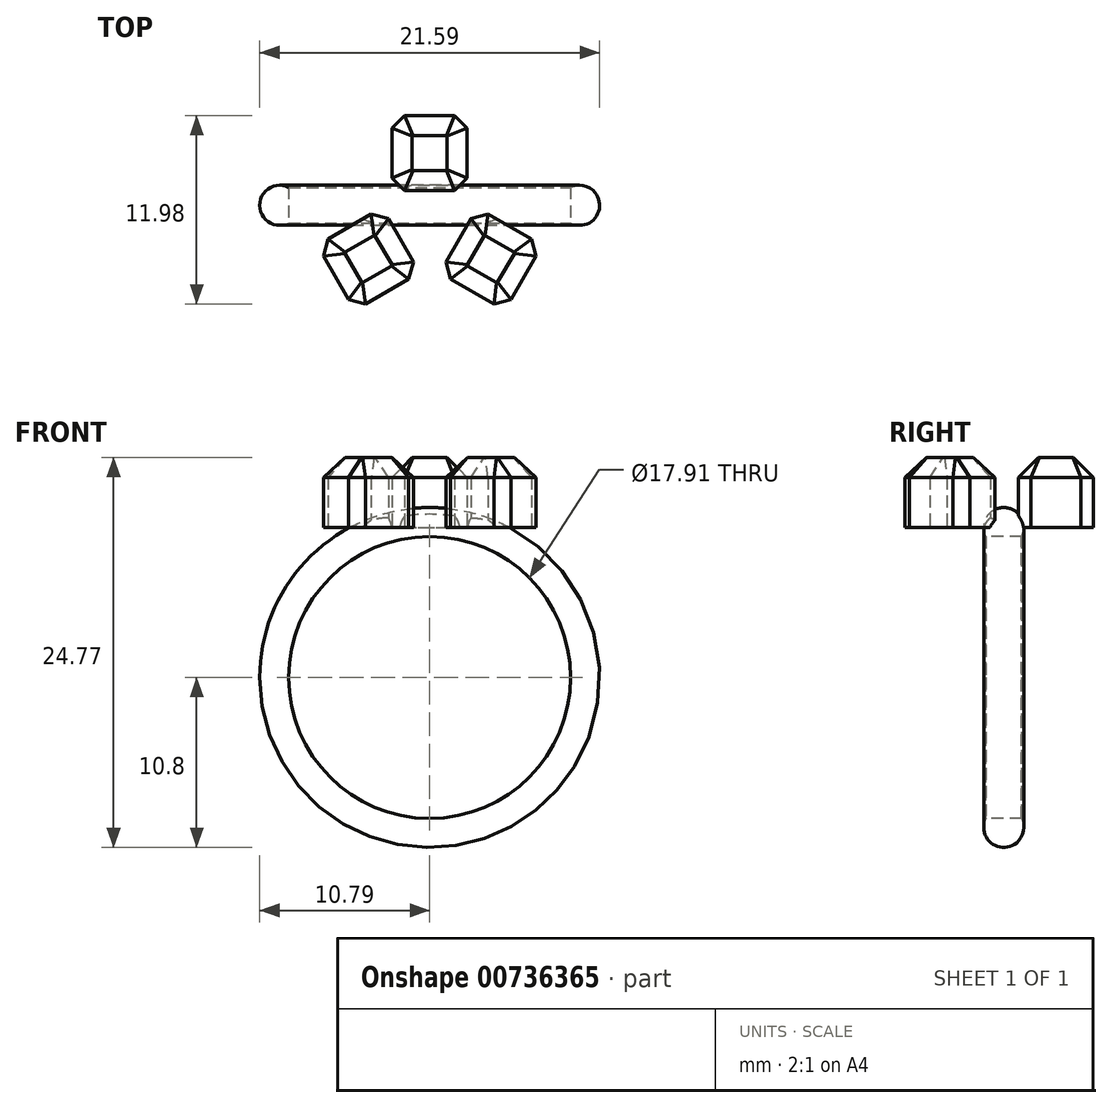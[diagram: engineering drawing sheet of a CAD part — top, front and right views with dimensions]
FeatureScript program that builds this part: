
annotation { "Feature Type Name" : "Feature", "Feature Type Description" : "" }
export const myFeature = defineFeature(function(context is Context, id is Id, definition is map)
    precondition{}
    {
        {
            var Q0;
            Q0=qCreatedBy(makeId("Front.planeOp"),FACE);
            var sketch = newSketch(context, id + "F0", { "sketchPlane" : qUnion([Q0])});
            skCircle(sketch, "E0", {"center": v(0, 0) * mm, "radius": 9.53 * mm});
            skSolve(sketch);
        }
        {
            var Q0;
            Q0=qCreatedBy(makeId("Top.planeOp"),FACE);
            var sketch = newSketch(context, id + "F1", { "sketchPlane" : qUnion([Q0])});
            skLineSegment(sketch, "E1", {"start": v(0, 0) * mm, "end": v(-9.52, 0) * mm});
            skArc(sketch, "E2", {"start": v(-8.95, 1.13) * mm, "mid": v(-10.8, 0) * mm, "end": v(-8.95, -1.13) * mm});
            skLineSegment(sketch, "E3", {"start": v(-8.95, 1.13) * mm, "end": v(-8.95, -1.13) * mm});
            skSolve(sketch);
        }
        {
            var Q0;
            Q0=makeQuery(id+"F1.imprint","IMPRINT",FACE,{"disambiguationData":[TD([[makeQuery(id+"F1.imprint","IMPRINT",EDGE,{"derivedFrom":sQuery(id+"F1.wireOp",EDGE,"E2")}),1.0]])]});
            var Q1;
            Q1=sQuery(id+"F0.wireOp",EDGE,"E0");
            sweep(context, id + "F2", {"profiles" : qUnion([Q0]), "path" : qUnion([Q1])});
        }
        {
            var Q0;
            Q0=qCreatedBy(makeId("Top.planeOp"),FACE);
            cPlane(context, id + "F3", {"entities" : qUnion([Q0]), "cplaneType" : CPlaneType.OFFSET, "offset" : 10.8 * mm, "width" : 152.4 * mm, "height" : 152.4 * mm});
        }
        {
            var Q0;
            Q0=qCreatedBy(id+"F3.planeOp",FACE);
            var sketch = newSketch(context, id + "F4", { "sketchPlane" : qUnion([Q0])});
            skCircle(sketch, "E4", {"center": v(0, -1.17) * mm, "radius": 2.12 * mm});
            skLineSegment(sketch, "E5", {"start": v(0, 0.95) * mm, "end": v(-1.59, 0.95) * mm});
            skLineSegment(sketch, "E6", {"start": v(-2.38, 1.74) * mm, "end": v(-2.38, 3.33) * mm});
            skLineSegment(sketch, "E7", {"start": v(-2.38, 3.33) * mm, "end": v(-2.38, 4.92) * mm});
            skLineSegment(sketch, "E8", {"start": v(-1.59, 5.71) * mm, "end": v(0, 5.71) * mm});
            skLineSegment(sketch, "E9", {"start": v(-1.59, 5.71) * mm, "end": v(-2.38, 4.92) * mm});
            skLineSegment(sketch, "E10", {"start": v(-2.38, 1.74) * mm, "end": v(-1.59, 0.95) * mm});
            skLineSegment(sketch, "E11.MirrorCS", {"start": v(0, 0.95) * mm, "end": v(1.59, 0.95) * mm});
            skLineSegment(sketch, "E12.MirrorCS", {"start": v(2.38, 1.74) * mm, "end": v(2.38, 3.33) * mm});
            skLineSegment(sketch, "E13.MirrorCS", {"start": v(2.38, 3.33) * mm, "end": v(2.38, 4.92) * mm});
            skLineSegment(sketch, "E14.MirrorCS", {"start": v(1.59, 5.71) * mm, "end": v(0, 5.71) * mm});
            skLineSegment(sketch, "E15.MirrorCS", {"start": v(1.59, 5.71) * mm, "end": v(2.38, 4.92) * mm});
            skLineSegment(sketch, "E16.MirrorCS", {"start": v(2.38, 1.74) * mm, "end": v(1.59, 0.95) * mm});
            skLineSegment(sketch, "E17.1.0", {"start": v(-3.7, -0.56) * mm, "end": v(-2.63, -0.85) * mm});
            skLineSegment(sketch, "E17.1.1", {"start": v(-6.75, -3.23) * mm, "end": v(-6.46, -2.14) * mm});
            skLineSegment(sketch, "E17.1.2", {"start": v(-6.75, -3.23) * mm, "end": v(-5.96, -4.6) * mm});
            skLineSegment(sketch, "E17.1.3", {"start": v(-5.08, -1.35) * mm, "end": v(-6.46, -2.14) * mm});
            skLineSegment(sketch, "E17.1.4", {"start": v(-3.7, -0.56) * mm, "end": v(-5.08, -1.35) * mm});
            skLineSegment(sketch, "E17.1.5", {"start": v(-1.83, -2.22) * mm, "end": v(-2.63, -0.85) * mm});
            skLineSegment(sketch, "E17.1.6", {"start": v(-1.33, -4.68) * mm, "end": v(-1.04, -3.6) * mm});
            skLineSegment(sketch, "E17.1.7", {"start": v(-5.16, -5.98) * mm, "end": v(-4.08, -6.27) * mm});
            skLineSegment(sketch, "E17.1.8", {"start": v(-5.16, -5.98) * mm, "end": v(-5.96, -4.6) * mm});
            skLineSegment(sketch, "E17.1.9", {"start": v(-2.7, -5.48) * mm, "end": v(-4.08, -6.27) * mm});
            skLineSegment(sketch, "E17.1.10", {"start": v(-1.33, -4.68) * mm, "end": v(-2.7, -5.48) * mm});
            skLineSegment(sketch, "E17.1.11", {"start": v(-1.83, -2.22) * mm, "end": v(-1.04, -3.6) * mm});
            skLineSegment(sketch, "E17.2.0", {"start": v(1.33, -4.68) * mm, "end": v(1.04, -3.6) * mm});
            skLineSegment(sketch, "E17.2.1", {"start": v(5.16, -5.98) * mm, "end": v(4.08, -6.27) * mm});
            skLineSegment(sketch, "E17.2.2", {"start": v(5.16, -5.98) * mm, "end": v(5.96, -4.6) * mm});
            skLineSegment(sketch, "E17.2.3", {"start": v(2.7, -5.48) * mm, "end": v(4.08, -6.27) * mm});
            skLineSegment(sketch, "E17.2.4", {"start": v(1.33, -4.68) * mm, "end": v(2.7, -5.48) * mm});
            skLineSegment(sketch, "E17.2.5", {"start": v(1.83, -2.22) * mm, "end": v(1.04, -3.6) * mm});
            skLineSegment(sketch, "E17.2.6", {"start": v(3.7, -0.56) * mm, "end": v(2.63, -0.85) * mm});
            skLineSegment(sketch, "E17.2.7", {"start": v(6.75, -3.23) * mm, "end": v(6.46, -2.14) * mm});
            skLineSegment(sketch, "E17.2.8", {"start": v(6.75, -3.23) * mm, "end": v(5.96, -4.6) * mm});
            skLineSegment(sketch, "E17.2.9", {"start": v(5.08, -1.35) * mm, "end": v(6.46, -2.14) * mm});
            skLineSegment(sketch, "E17.2.10", {"start": v(3.7, -0.56) * mm, "end": v(5.08, -1.35) * mm});
            skLineSegment(sketch, "E17.2.11", {"start": v(1.83, -2.22) * mm, "end": v(2.63, -0.85) * mm});
            skSolve(sketch);
        }
        {
            var Q0;
            Q0=makeQuery(id+"F4.imprint","IMPRINT",FACE,{"disambiguationData":[TD([[makeQuery(id+"F4.imprint","IMPRINT",EDGE,{"derivedFrom":sQuery(id+"F4.wireOp",EDGE,"E5")}),-1.0]])]});
            var Q1;
            Q1=makeQuery(id+"F4.imprint","IMPRINT",FACE,{"disambiguationData":[TD([[makeQuery(id+"F4.imprint","IMPRINT",EDGE,{"derivedFrom":sQuery(id+"F4.wireOp",EDGE,"E17.1.0")}),-1.0]])]});
            var Q2;
            Q2=makeQuery(id+"F4.imprint","IMPRINT",FACE,{"disambiguationData":[TD([[makeQuery(id+"F4.imprint","IMPRINT",EDGE,{"derivedFrom":sQuery(id+"F4.wireOp",EDGE,"E17.2.0")}),-1.0]])]});
            extrude(context, id + "F5", {"entities" : qUnion([Q0, Q1, Q2]), "depth" : 3.17 * mm, "offsetDistance" : 25.4 * mm});
        }
        {
            var Q0;
            Q0=makeQuery(id+"F5.opExtrude","CAP_FACE",FACE,{"disambiguationData":[OSD([sQuery(id+"F4.wireOp",EDGE,"E17.1.0"),sQuery(id+"F4.wireOp",EDGE,"E17.1.1"),sQuery(id+"F4.wireOp",EDGE,"E17.1.2"),sQuery(id+"F4.wireOp",EDGE,"E17.1.3"),sQuery(id+"F4.wireOp",EDGE,"E17.1.4"),sQuery(id+"F4.wireOp",EDGE,"E17.1.5"),sQuery(id+"F4.wireOp",EDGE,"E17.1.6"),sQuery(id+"F4.wireOp",EDGE,"E17.1.7"),sQuery(id+"F4.wireOp",EDGE,"E17.1.8"),sQuery(id+"F4.wireOp",EDGE,"E17.1.9"),sQuery(id+"F4.wireOp",EDGE,"E17.1.10"),sQuery(id+"F4.wireOp",EDGE,"E17.1.11")])],"isStart":false});
            var Q1;
            Q1=makeQuery(id+"F5.opExtrude","CAP_FACE",FACE,{"disambiguationData":[OSD([sQuery(id+"F4.wireOp",EDGE,"E5"),sQuery(id+"F4.wireOp",EDGE,"E6"),sQuery(id+"F4.wireOp",EDGE,"E7"),sQuery(id+"F4.wireOp",EDGE,"E8"),sQuery(id+"F4.wireOp",EDGE,"E9"),sQuery(id+"F4.wireOp",EDGE,"E10"),sQuery(id+"F4.wireOp",EDGE,"E11.MirrorCS"),sQuery(id+"F4.wireOp",EDGE,"E12.MirrorCS"),sQuery(id+"F4.wireOp",EDGE,"E13.MirrorCS"),sQuery(id+"F4.wireOp",EDGE,"E14.MirrorCS"),sQuery(id+"F4.wireOp",EDGE,"E15.MirrorCS"),sQuery(id+"F4.wireOp",EDGE,"E16.MirrorCS")])],"isStart":false});
            var Q2;
            Q2=makeQuery(id+"F5.opExtrude","CAP_FACE",FACE,{"disambiguationData":[OSD([sQuery(id+"F4.wireOp",EDGE,"E17.2.0"),sQuery(id+"F4.wireOp",EDGE,"E17.2.1"),sQuery(id+"F4.wireOp",EDGE,"E17.2.2"),sQuery(id+"F4.wireOp",EDGE,"E17.2.3"),sQuery(id+"F4.wireOp",EDGE,"E17.2.4"),sQuery(id+"F4.wireOp",EDGE,"E17.2.5"),sQuery(id+"F4.wireOp",EDGE,"E17.2.6"),sQuery(id+"F4.wireOp",EDGE,"E17.2.7"),sQuery(id+"F4.wireOp",EDGE,"E17.2.8"),sQuery(id+"F4.wireOp",EDGE,"E17.2.9"),sQuery(id+"F4.wireOp",EDGE,"E17.2.10"),sQuery(id+"F4.wireOp",EDGE,"E17.2.11")])],"isStart":false});
            chamfer(context, id + "F6", {"entities" : qUnion([Q0, Q1, Q2]), "width" : 1.27 * mm, "tangentPropagation" : true});
        }
        {
            var Q0;
            Q0=makeQuery(id+"F4.imprint","IMPRINT",FACE,{"disambiguationData":[TD([[makeQuery(id+"F4.imprint","IMPRINT",EDGE,{"derivedFrom":sQuery(id+"F4.wireOp",EDGE,"E17.2.0")}),-1.0]])]});
            var Q1;
            Q1=makeQuery(id+"F4.imprint","IMPRINT",FACE,{"disambiguationData":[TD([[makeQuery(id+"F4.imprint","IMPRINT",EDGE,{"derivedFrom":sQuery(id+"F4.wireOp",EDGE,"E17.1.0")}),-1.0]])]});
            var Q2;
            Q2=makeQuery(id+"F4.imprint","IMPRINT",FACE,{"disambiguationData":[TD([[makeQuery(id+"F4.imprint","IMPRINT",EDGE,{"derivedFrom":sQuery(id+"F4.wireOp",EDGE,"E5")}),-1.0]])]});
            extrude(context, id + "F7", {"entities" : qUnion([Q0, Q1, Q2]), "operationType" : NewBodyOperationType.ADD, "oppositeDirection" : true, "depth" : 1.27 * mm, "offsetDistance" : 25.4 * mm});
        }
        {
            var Q0;
            Q0=qCreatedBy(makeId("Front.planeOp"),FACE);
            var sketch = newSketch(context, id + "F8", { "sketchPlane" : qUnion([Q0])});
            skLineSegment(sketch, "E18", {"start": v(0, 75.88) * mm, "end": v(0, 56.87) * mm});
            skSolve(sketch);
        }
    });
